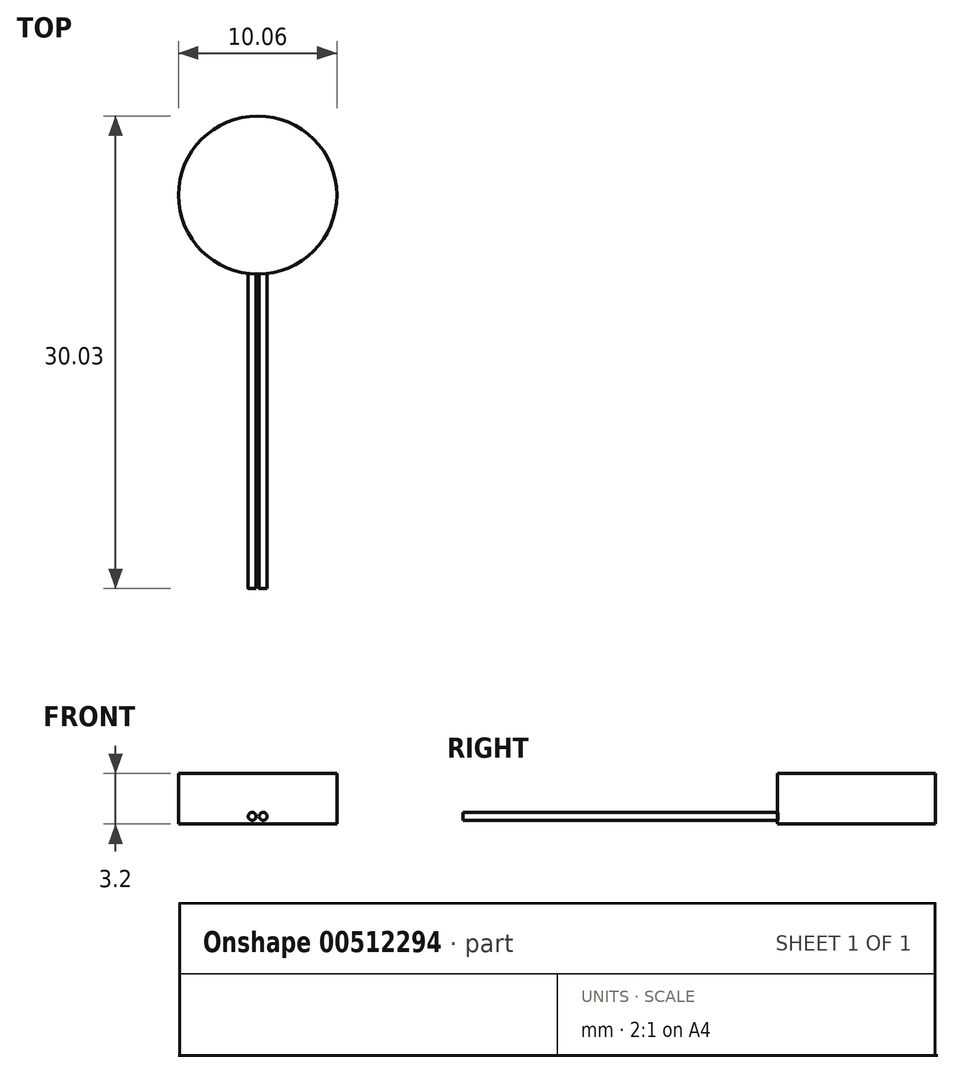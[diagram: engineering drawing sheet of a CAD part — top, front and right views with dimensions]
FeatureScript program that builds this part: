
annotation { "Feature Type Name" : "Feature", "Feature Type Description" : "" }
export const myFeature = defineFeature(function(context is Context, id is Id, definition is map)
    precondition{}
    {
        {
            var Q0;
            Q0=qCreatedBy(makeId("Top.planeOp"),FACE);
            var sketch = newSketch(context, id + "F0", { "sketchPlane" : qUnion([Q0])});
            skCircle(sketch, "E0", {"center": v(0, 0) * mm, "radius": 5.03 * mm});
            skSolve(sketch);
        }
        {
            var Q0;
            Q0 = qSketchRegion(id + "F0", true);
            extrude(context, id + "F1", {"entities" : qUnion([Q0]), "depth" : 3.2 * mm, "offsetDistance" : 25 * mm});
        }
        {
            var Q0;
            Q0=qCreatedBy(makeId("Front.planeOp"),FACE);
            var sketch = newSketch(context, id + "F2", { "sketchPlane" : qUnion([Q0])});
            skLineSegment(sketch, "E1", {"start": v(-0.35, 0.49) * mm, "end": v(0.35, 0.49) * mm, "construction": true});
            skCircle(sketch, "E2", {"center": v(-0.35, 0.49) * mm, "radius": 0.25 * mm});
            skCircle(sketch, "E3", {"center": v(0.35, 0.49) * mm, "radius": 0.25 * mm});
            skSolve(sketch);
        }
        {
            var Q0;
            Q0 = qSketchRegion(id + "F2", true);
            extrude(context, id + "F3", {"entities" : qUnion([Q0]), "operationType" : NewBodyOperationType.ADD, "depth" : 25 * mm, "offsetDistance" : 25 * mm});
        }
    });
